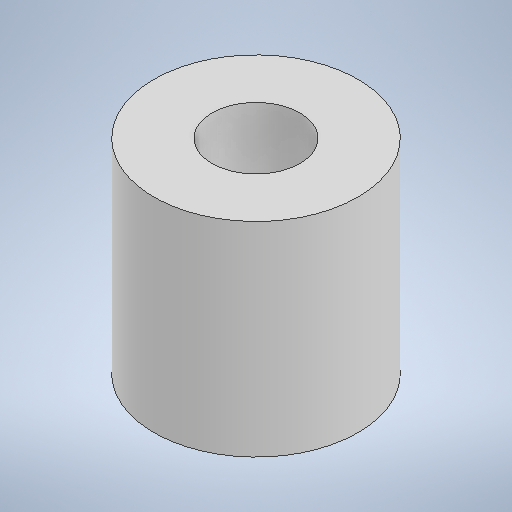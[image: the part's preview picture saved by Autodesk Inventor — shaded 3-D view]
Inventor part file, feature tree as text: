
AUTODESK INVENTOR PART (.ipt)
format: ipt  version: 2025.2 (Build 292293000, 293)  size: 190,976 bytes
history: native  units: mm
features: extrude x1, sketch x1
ambient origin geometry x8: Origin, YZ Plane, XZ Plane, XY Plane, X Axis, Y Axis, Z Axis, Center Point
bodies: Solid1 (feature_tree)
feature tree (2):
  extrude  "Extrusion1"  Depth=10.0mm
  sketch  "Sketch1"  dims[d0=4.3mm d1=10.0mm d2=10.0mm d3=0.0mm]
